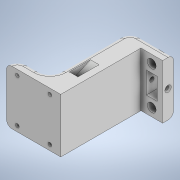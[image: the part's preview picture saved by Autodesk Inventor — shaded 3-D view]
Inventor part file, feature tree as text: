
AUTODESK INVENTOR PART (.ipt)
format: ipt  version: 2022.3 (Build 263350000, 350)  size: 310,272 bytes
history: native  units: mm
features: sketch x11, extrude x5, fillet x3, hole x3, sweep x2, projected_geometry x1
ambient origin geometry x8: Origin, YZ Plane, XZ Plane, XY Plane, X Axis, Y Axis, Z Axis, Center Point
bodies: Solid1 (feature_tree)
feature tree (25):
  extrude  "Extrusion1"  Depth=10.0mm
  fillet  "Fillet1"  Radius=50.0mm
  fillet  "Fillet2"  Radius=10.0mm
  fillet  "Fillet3"  Radius=40.0mm
  extrude  "Extrusion2"  Depth=10.0mm TaperAngle=0.0deg
  hole  "Hole1"  [1 undecoded]
  sweep  "Sweep1"
  sweep  "Sweep2"
  sketch  "Sketch8"  dims[d18=5.0mm d19=3.4mm]
  extrude  "Extrusion3"  Depth=40.0mm
  extrude  "Extrusion4"  Depth=40.0mm
  extrude  "Extrusion5"  Depth=3.4mm
  hole  "Hole2"  [1 undecoded]
  hole  "Hole3"  [1 undecoded]
  sketch  "Sketch1"  dims[d0=20.0mm d1=74.0mm d2=50.0mm d3=10.0mm d4=40.0mm]
  sketch  "Sketch2"  dims[d5=10.0mm d6=50.0mm d7=0.0mm]
  sketch  "Sketch3"  dims[d8=10.0mm d9=5.0mm]
  sketch  "Sketch4"  dims[d10=10.0mm d11=10.0mm]
  sketch  "Sketch5"  dims[d12=5.0mm d13=10.0mm]
  sketch  "Sketch6"  dims[d14=5.0mm d15=40.0mm]
  sketch  "Sketch7"  dims[d16=5.0mm d17=40.0mm]
  sketch  "Sketch9"  dims[d20=3.4mm d21=3.4mm]
  sketch  "Sketch10"  dims[d22=3.4mm d23=50.0mm d24=0.0mm]
  projected_geometry  "Projected Loop1"
  sketch  "Sketch11"  dims[d25=3.4mm d26=6.0mm d27=6.0mm d28=2.0mm d29=90.0deg d30=2.2mm d31=0.0mm d32=8.0mm d33=8.0mm d34=20.0mm d35=5.0mm d36=20.0mm d37=9.0mm d38=0.0mm d39=0.0mm d40=0.0mm d41=0.0mm d42=8.0mm d43=8.0mm d44=20.0mm d45=5.0mm d46=20.0mm d47=9.0mm d48=0.0mm d49=0.0mm d50=10.0mm d51=20.0mm d52=8.0mm d53=8.0mm d54=5.0mm d55=0.0mm d56=0.0mm d57=0.0mm d58=12.0mm d59=12.0mm d60=2.0mm d61=0.0mm d62=3.4mm d63=6.0mm d64=5.9mm d65=2.0mm d66=90.0deg d67=5.0mm d68=0.0mm d69=3.4mm d70=6.0mm d71=4.1mm d72=5.1mm d73=90.0deg d74=6.9mm d75=0.0mm]
note: 3 required parameter values undecoded (feature->parameter linkage not recoverable at this tier; creation-order binding heuristic only, values carry confidence <= 0.55)
